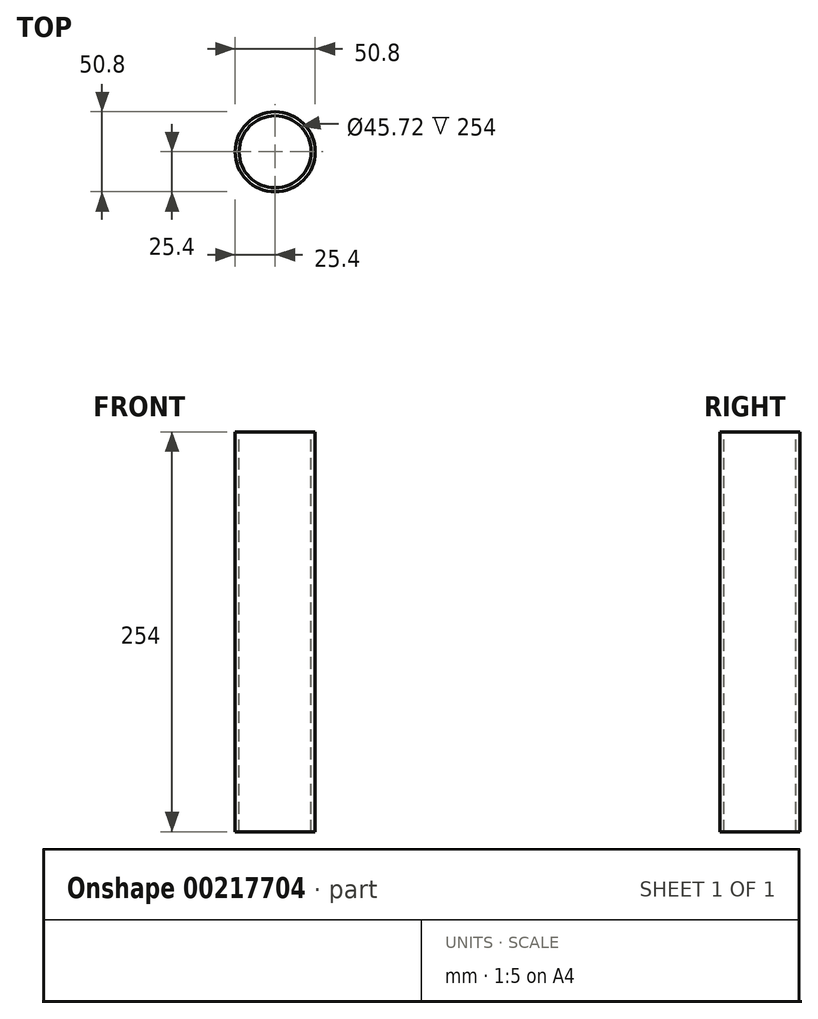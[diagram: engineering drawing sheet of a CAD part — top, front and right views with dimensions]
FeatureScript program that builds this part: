
annotation { "Feature Type Name" : "Feature", "Feature Type Description" : "" }
export const myFeature = defineFeature(function(context is Context, id is Id, definition is map)
    precondition{}
    {
        {
            var Q0;
            Q0=qCreatedBy(makeId("Top.planeOp"),FACE);
            var sketch = newSketch(context, id + "F0", { "sketchPlane" : qUnion([Q0])});
            skCircle(sketch, "E0", {"center": v(0, 0) * mm, "radius": 25.4 * mm});
            skPoint(sketch, "E1", {"position": v(0, 25.4) * mm});
            skPoint(sketch, "E2", {"position": v(0, -25.4) * mm});
            skPoint(sketch, "E3", {"position": v(1.94, 0) * mm});
            skSolve(sketch);
        }
        {
            var Q0;
            Q0=makeQuery(id+"F0.imprint","IMPRINT",FACE,{"disambiguationData":[TD([[makeQuery(id+"F0.imprint","IMPRINT",EDGE,{"derivedFrom":sQuery(id+"F0.wireOp",EDGE,"E0")}),1.0]])]});
            extrude(context, id + "F1", {"entities" : qUnion([Q0]), "endBound" : BoundingType.SYMMETRIC, "depth" : 254 * mm});
        }
        {
            var Q0;
            Q0=makeQuery(id+"F1.opExtrude","CAP_FACE",FACE,{"disambiguationData":[OSD([sQuery(id+"F0.wireOp",EDGE,"E0")])],"isStart":false});
            var sketch = newSketch(context, id + "F2", { "sketchPlane" : qUnion([Q0])});
            skCircle(sketch, "E4", {"center": v(0, 0) * mm, "radius": 22.86 * mm});
            skPoint(sketch, "E5", {"position": v(0, 22.86) * mm});
            skPoint(sketch, "E6", {"position": v(0, -22.86) * mm});
            skSolve(sketch);
        }
        {
            var Q0;
            Q0=sQuery(id+"F2.wireOp",VERTEX,"E4.center");
            var Q1;
            Q1=makeQuery(id+"F1.opExtrude","SWEPT_BODY",BODY,{"disambiguationData":[OSD([sQuery(id+"F0.wireOp",EDGE,"E0")])]});
            hole(context, id + "F3", {"style" : HoleStyle.SIMPLE, "endStyle" : HoleEndStyle.THROUGH, "holeDiameter" : 45.72 * mm, "startFromSketch" : true, "locations" : qUnion([Q0]), "scope" : qUnion([Q1]), "isTappedThrough" : true});
        }
    });
